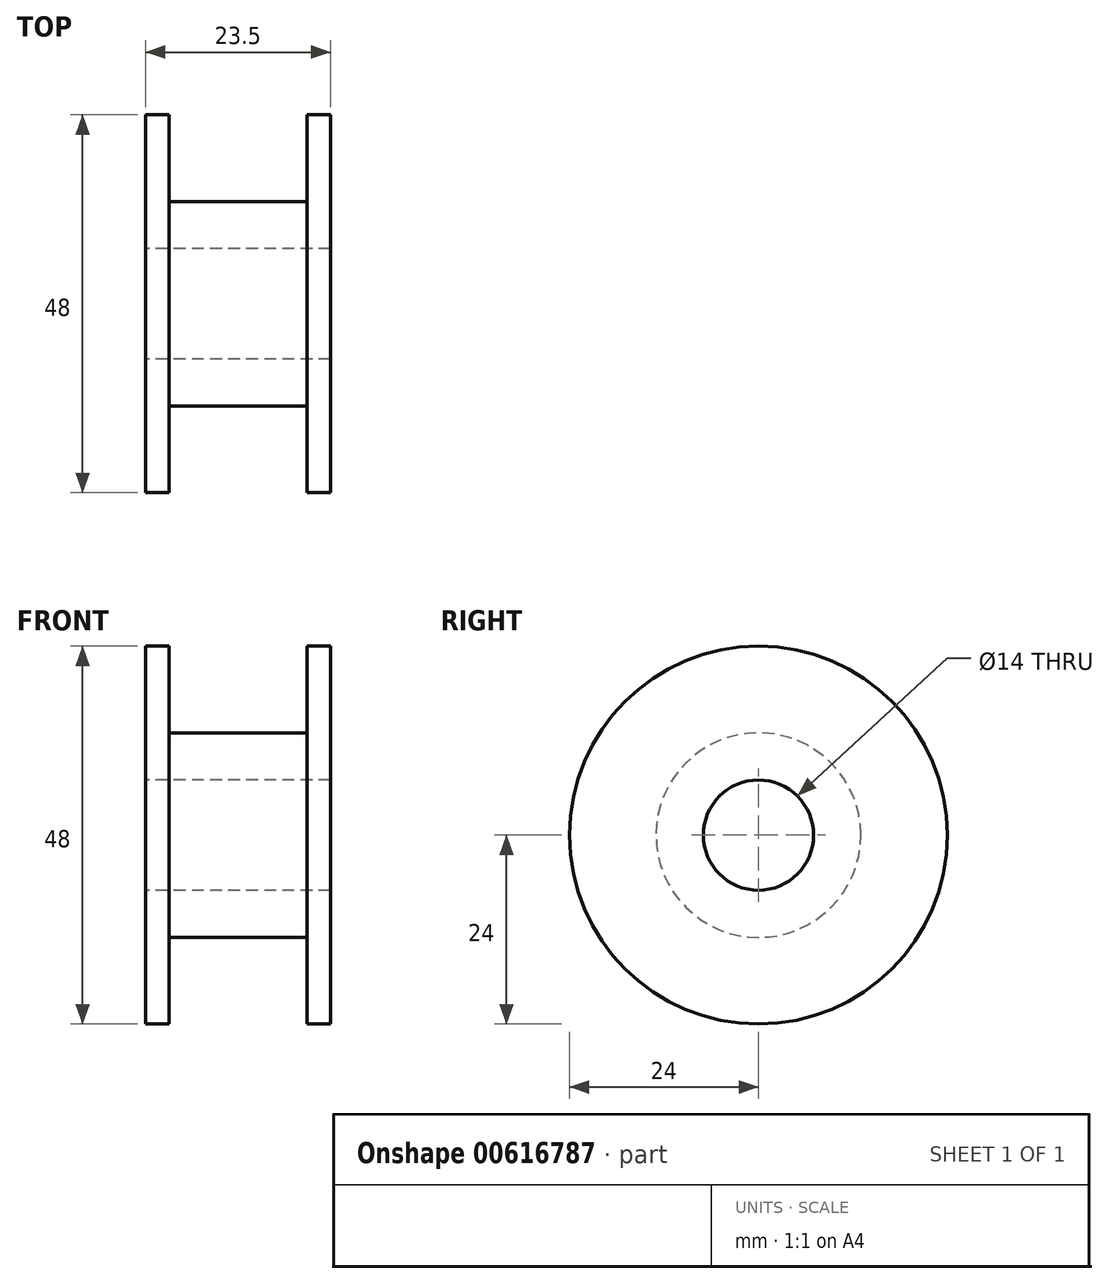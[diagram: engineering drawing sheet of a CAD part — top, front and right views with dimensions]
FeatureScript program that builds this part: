
annotation { "Feature Type Name" : "Feature", "Feature Type Description" : "" }
export const myFeature = defineFeature(function(context is Context, id is Id, definition is map)
    precondition{}
    {
        {
            var Q0;
            Q0=qCreatedBy(makeId("Front.planeOp"),FACE);
            var sketch = newSketch(context, id + "F0", { "sketchPlane" : qUnion([Q0])});
            skLineSegment(sketch, "E0", {"start": v(0, 24) * mm, "end": v(0, 7) * mm});
            skLineSegment(sketch, "E1", {"start": v(0, 7) * mm, "end": v(23.5, 7) * mm});
            skLineSegment(sketch, "E2", {"start": v(23.5, 7) * mm, "end": v(23.5, 24) * mm});
            skLineSegment(sketch, "E3", {"start": v(23.5, 24) * mm, "end": v(20.5, 24) * mm});
            skLineSegment(sketch, "E4", {"start": v(20.5, 24) * mm, "end": v(20.5, 13) * mm});
            skLineSegment(sketch, "E5", {"start": v(20.5, 13) * mm, "end": v(3, 13) * mm});
            skLineSegment(sketch, "E6", {"start": v(3, 13) * mm, "end": v(3, 24) * mm});
            skLineSegment(sketch, "E7", {"start": v(3, 24) * mm, "end": v(0, 24) * mm});
            skLineSegment(sketch, "E8", {"start": v(0, 0) * mm, "end": v(30.46, 0) * mm, "construction": true});
            skSolve(sketch);
        }
        {
            var Q0;
            Q0=makeQuery(id+"F0.imprint","IMPRINT",FACE,{"disambiguationData":[TD([[makeQuery(id+"F0.imprint","IMPRINT",EDGE,{"derivedFrom":sQuery(id+"F0.wireOp",EDGE,"E0")}),1.0]])]});
            var Q1;
            Q1=sQuery(id+"F0.wireOp",EDGE,"E8");
            revolve(context, id + "F1", {"surfaceOperationType" : NewSurfaceOperationType.NEW, "entities" : qUnion([Q0]), "axis" : qUnion([Q1]), "revolveType" : RevolveType.FULL});
        }
    });
